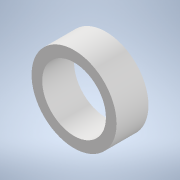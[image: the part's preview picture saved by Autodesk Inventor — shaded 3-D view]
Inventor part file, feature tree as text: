
AUTODESK INVENTOR PART (.ipt)
format: ipt  version: 2022 (Build 260153000, 153)  size: 100,352 bytes
history: native  units: mm
features: extrude x1, sketch x1
ambient origin geometry x8: Origin, YZ Plane, XZ Plane, XY Plane, X Axis, Y Axis, Z Axis, Center Point
bodies: Solid1 (feature_tree)
feature tree (2):
  extrude  "Extrusion1"  Depth=3.0mm
  sketch  "Sketch1"  dims[d0=6.0mm d1=8.0mm d2=3.0mm d3=0.0mm]
